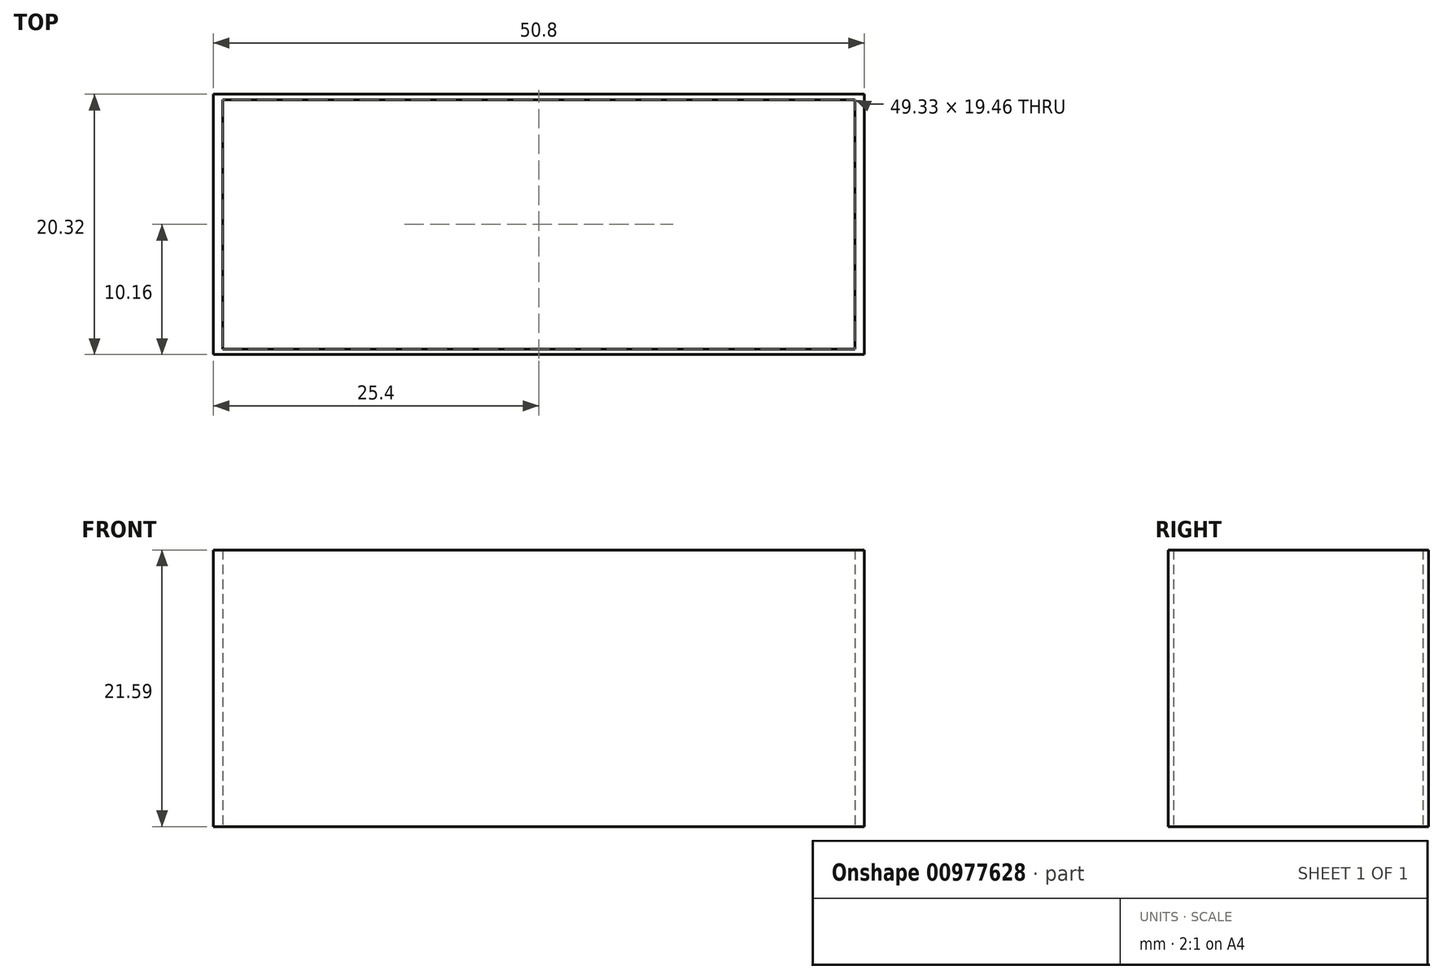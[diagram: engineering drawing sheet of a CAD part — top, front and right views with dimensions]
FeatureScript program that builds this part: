
annotation { "Feature Type Name" : "Feature", "Feature Type Description" : "" }
export const myFeature = defineFeature(function(context is Context, id is Id, definition is map)
    precondition{}
    {
        {
            var Q0;
            Q0=qCreatedBy(makeId("Top.planeOp"),FACE);
            var sketch = newSketch(context, id + "F0", { "sketchPlane" : qUnion([Q0])});
            skLineSegment(sketch, "E0.bottom", {"start": v(0, 0) * mm, "end": v(-50.8, 0) * mm});
            skLineSegment(sketch, "E0.top", {"start": v(0, -20.32) * mm, "end": v(-50.8, -20.32) * mm});
            skLineSegment(sketch, "E0.left", {"start": v(0, 0) * mm, "end": v(0, -20.32) * mm});
            skLineSegment(sketch, "E0.right", {"start": v(-50.8, 0) * mm, "end": v(-50.8, -20.32) * mm});
            skPoint(sketch, "E1", {"position": v(-25.4, 0) * mm});
            skPoint(sketch, "E2", {"position": v(0, -10.16) * mm});
            skPoint(sketch, "E3", {"position": v(-25.4, -10.16) * mm});
            skLineSegment(sketch, "E4.bottom", {"start": v(-50.06, -0.43) * mm, "end": v(-0.74, -0.43) * mm});
            skLineSegment(sketch, "E4.top", {"start": v(-50.06, -19.89) * mm, "end": v(-0.74, -19.89) * mm});
            skLineSegment(sketch, "E4.left", {"start": v(-50.06, -0.43) * mm, "end": v(-50.06, -19.89) * mm});
            skLineSegment(sketch, "E4.right", {"start": v(-0.74, -0.43) * mm, "end": v(-0.74, -19.89) * mm});
            skPoint(sketch, "E5", {"position": v(-25.4, -0.43) * mm});
            skPoint(sketch, "E6", {"position": v(-50.06, -10.16) * mm});
            skSolve(sketch);
        }
        {
            var Q0;
            Q0=makeQuery(id+"F0.imprint","IMPRINT",FACE,{"disambiguationData":[TD([[makeQuery(id+"F0.imprint","IMPRINT",EDGE,{"derivedFrom":sQuery(id+"F0.wireOp",EDGE,"E0.bottom")}),1.0]])]});
            extrude(context, id + "F1", {"entities" : qUnion([Q0]), "depth" : 21.59 * mm, "offsetDistance" : 25.4 * mm});
        }
    });
